# Revit family: Bookcase_Multi-Shelf
name_source: partatom
category: Generic Models
units: mm (PartAtom-declared; Revit-internal decimal feet)

## family parameters
Always vertical = Yes
Can host rebar = No
Classification Number = 23.40.20.24.34
Cut with Voids When Loaded = No
Maintain Annotation Orientation = No
Part Type = Normal
Room Calculation Point = No
Round Connector Dimension = Use Diameter
Shared = No
Work Plane-Based = No

## types (6) — shared parameters
Assembly Code = E2020200
Body Material = ARCAT - Wood - Oak_Red
Construction Details = http://www.arcat.com
Default Elevation = 0' - 0"
Green Building-LEED = http://www.arcat.com
Keynote = 12500
Maintenance Schedule (Months) = 5
Manufacturer = Generic
Manufacturer Fax = (203) 939-2444
Manufacturer Website = http://www.arcat.com
Model = Generic
Product Data = http://www.arcat.com
Product Properties = http://www.arcat.com
Shelf Material = ARCAT - Wood - Oak_Red
Specification = http://www.arcat.com
Warranty Duration (Years) = 5
shlfdpth = 0' - 7 3/8"
shlfwdth = 3' - 10 3/4"
zero-valued in all types: Expected Lifespan (Years)

## per-type parameters (varying)
| type | Description |
| 4x4 -  5 Shelf | 4' x 4' Bookcase - 5 Shelves |
| 4x4 -  4 Shelf | 4' x 4' Bookcase - 4 Shelves |
| 4x4 -  3 Shelf | 4' x 4' Bookcase - 3 Shelves |
| 4x6 - 3 Shelves | 4' x 6' Bookcase - 3 Shelves |
| 4x6 - 4 Shelves | 4' x 6' Bookcase - 4 Shelves |
| 4x6 - 5 Shelves | 4' x 6' Bookcase - 5 Shelves |

## geometry (parser evidence)
native form markers: Blend x2, Sweep x5
no freeform markers — native parametric forms only
